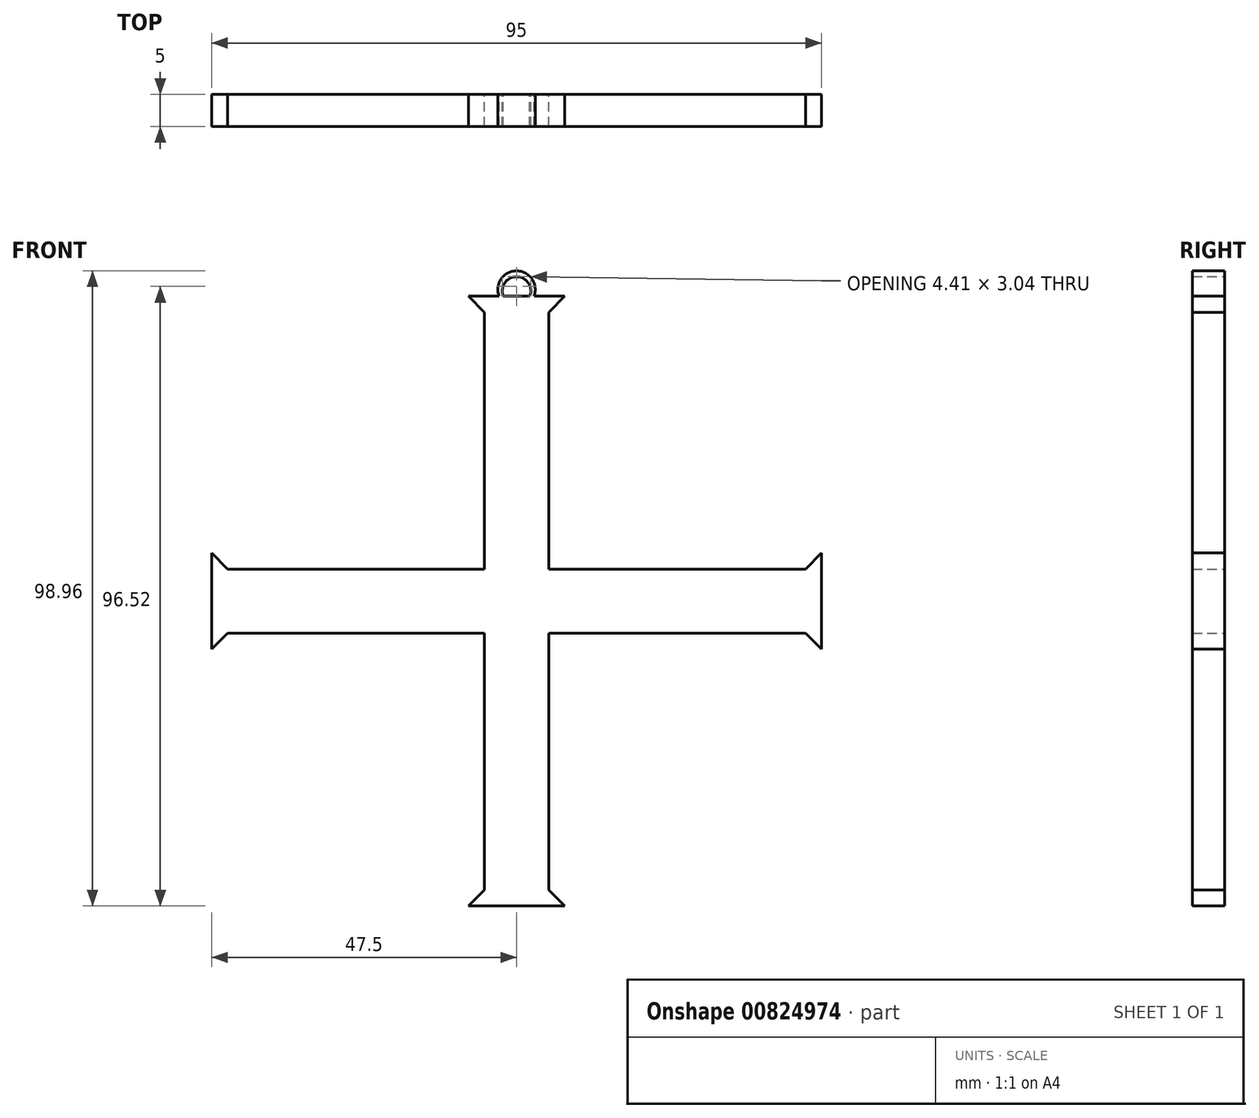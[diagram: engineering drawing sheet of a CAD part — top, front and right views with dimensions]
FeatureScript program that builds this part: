
annotation { "Feature Type Name" : "Feature", "Feature Type Description" : "" }
export const myFeature = defineFeature(function(context is Context, id is Id, definition is map)
    precondition{}
    {
        {
            var Q0;
            Q0=qCreatedBy(makeId("Front.planeOp"),FACE);
            var sketch = newSketch(context, id + "F0", { "sketchPlane" : qUnion([Q0])});
            skLineSegment(sketch, "E0", {"start": v(10, 50) * mm, "end": v(10, 10) * mm});
            skLineSegment(sketch, "E1", {"start": v(10, 10) * mm, "end": v(50, 10) * mm});
            skLineSegment(sketch, "E2", {"start": v(50, 0) * mm, "end": v(10, 0) * mm});
            skLineSegment(sketch, "E3", {"start": v(10, 0) * mm, "end": v(10, -40) * mm});
            skLineSegment(sketch, "E4", {"start": v(10, -40) * mm, "end": v(0, -40) * mm});
            skLineSegment(sketch, "E5", {"start": v(0, -40) * mm, "end": v(0, 0) * mm});
            skLineSegment(sketch, "E6", {"start": v(0, 0) * mm, "end": v(-40, 0) * mm});
            skLineSegment(sketch, "E7", {"start": v(-40, 10) * mm, "end": v(0, 10) * mm});
            skLineSegment(sketch, "E8", {"start": v(0, 10) * mm, "end": v(0, 50) * mm});
            skLineSegment(sketch, "E9", {"start": v(-40, 10) * mm, "end": v(-42.5, 12.5) * mm});
            skLineSegment(sketch, "E10", {"start": v(-42.5, 12.5) * mm, "end": v(-42.5, -2.5) * mm});
            skLineSegment(sketch, "E11", {"start": v(-42.5, -2.5) * mm, "end": v(-40, 0) * mm});
            skLineSegment(sketch, "E12", {"start": v(0, -40) * mm, "end": v(-2.5, -42.5) * mm});
            skLineSegment(sketch, "E13", {"start": v(-2.5, -42.5) * mm, "end": v(12.5, -42.5) * mm});
            skLineSegment(sketch, "E14", {"start": v(12.5, -42.5) * mm, "end": v(10, -40) * mm});
            skLineSegment(sketch, "E15", {"start": v(50, 10) * mm, "end": v(52.5, 12.5) * mm});
            skLineSegment(sketch, "E16", {"start": v(52.5, 12.5) * mm, "end": v(52.5, -2.5) * mm});
            skLineSegment(sketch, "E17", {"start": v(52.5, -2.5) * mm, "end": v(50, 0) * mm});
            skLineSegment(sketch, "E18", {"start": v(0, 50) * mm, "end": v(-2.5, 52.5) * mm});
            skLineSegment(sketch, "E19", {"start": v(-2.5, 52.5) * mm, "end": v(2.3, 52.5) * mm});
            skLineSegment(sketch, "E20", {"start": v(12.5, 52.5) * mm, "end": v(10, 50) * mm});
            skArc(sketch, "E21", {"start": v(7.06, 52.5) * mm, "mid": v(5, 55.54) * mm, "end": v(2.94, 52.5) * mm});
            skArc(sketch, "E22", {"start": v(7.7, 52.5) * mm, "mid": v(5, 56.46) * mm, "end": v(2.3, 52.5) * mm});
            skLineSegment(sketch, "E23", {"start": v(2.3, 52.5) * mm, "end": v(-2.5, 52.5) * mm});
            skLineSegment(sketch, "E24", {"start": v(7.7, 52.5) * mm, "end": v(12.5, 52.5) * mm});
            skLineSegment(sketch, "E25", {"start": v(7.7, 52.5) * mm, "end": v(7.06, 52.5) * mm});
            skLineSegment(sketch, "E26.trimOffspring", {"start": v(2.94, 52.5) * mm, "end": v(7.06, 52.5) * mm});
            skLineSegment(sketch, "E27", {"start": v(2.3, 52.5) * mm, "end": v(2.94, 52.5) * mm});
            skPoint(sketch, "E28", {"position": v(5, 52.5) * mm});
            skSolve(sketch);
        }
        {
            var Q0;
            Q0 = qSketchRegion(id + "F0", true);
            extrude(context, id + "F1", {"entities" : qUnion([Q0]), "depth" : 5 * mm, "offsetDistance" : 25 * mm});
        }
    });
